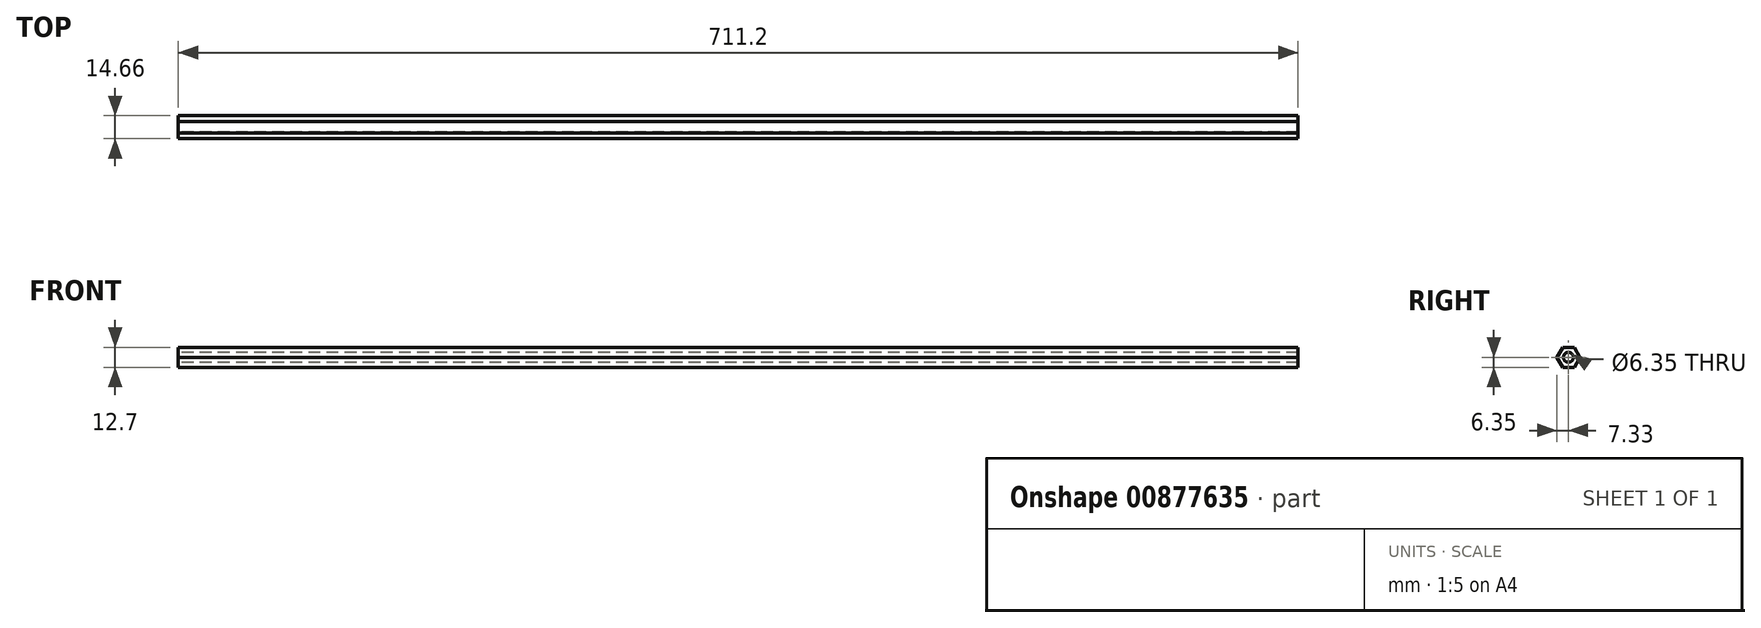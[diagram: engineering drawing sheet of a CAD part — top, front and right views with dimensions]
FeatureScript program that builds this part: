
annotation { "Feature Type Name" : "Feature", "Feature Type Description" : "" }
export const myFeature = defineFeature(function(context is Context, id is Id, definition is map)
    precondition{}
    {
        {
            var Q0;
            Q0=qCreatedBy(makeId("Right.planeOp"),FACE);
            var sketch = newSketch(context, id + "F0", { "sketchPlane" : qUnion([Q0])});
            skCircle(sketch, "E0.cCircle", {"center": v(0, 0) * mm, "radius": 6.35 * mm, "construction": true});
            skLineSegment(sketch, "E0.0", {"start": v(-3.67, 6.35) * mm, "end": v(3.67, 6.35) * mm});
            skLineSegment(sketch, "E0.1", {"start": v(3.67, 6.35) * mm, "end": v(7.33, 0) * mm});
            skLineSegment(sketch, "E0.2", {"start": v(7.33, 0) * mm, "end": v(3.67, -6.35) * mm});
            skLineSegment(sketch, "E0.3", {"start": v(3.67, -6.35) * mm, "end": v(-3.67, -6.35) * mm});
            skLineSegment(sketch, "E0.4", {"start": v(-3.67, -6.35) * mm, "end": v(-7.33, 0) * mm});
            skLineSegment(sketch, "E0.5", {"start": v(-7.33, 0) * mm, "end": v(-3.67, 6.35) * mm});
            skPoint(sketch, "E0.0.midPoint", {"position": v(0, 6.35) * mm});
            skCircle(sketch, "E1", {"center": v(0, 0) * mm, "radius": 3.18 * mm});
            skSolve(sketch);
        }
        {
            var Q0;
            Q0 = qSketchRegion(id + "F0", true);
            extrude(context, id + "F1", {"entities" : qUnion([Q0]), "depth" : 711.2 * mm, "offsetDistance" : 25.4 * mm});
        }
    });
